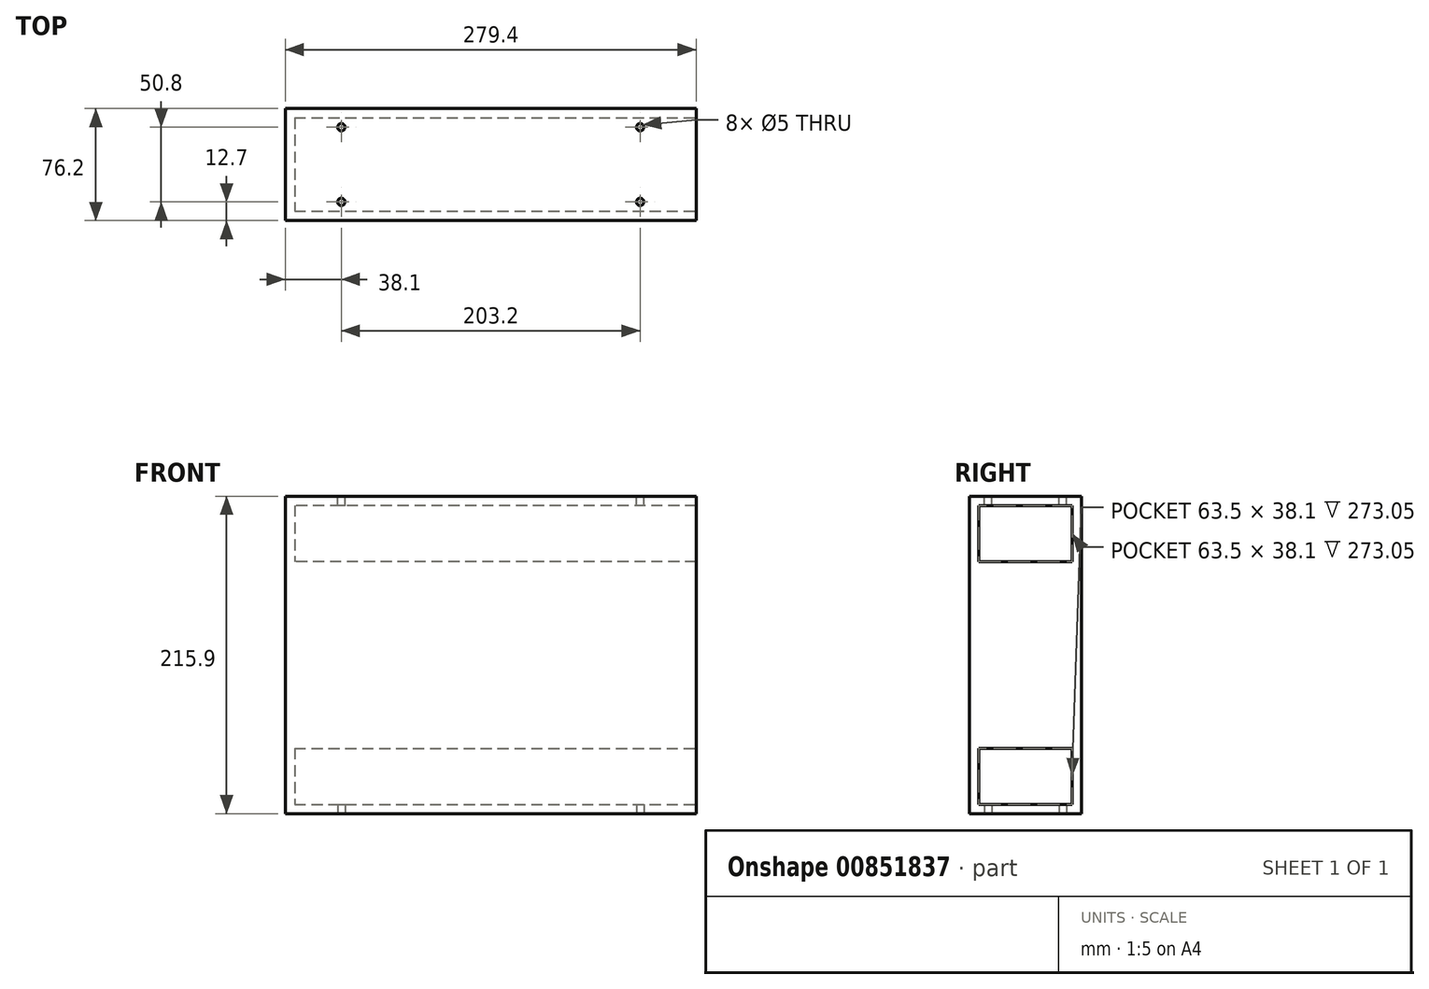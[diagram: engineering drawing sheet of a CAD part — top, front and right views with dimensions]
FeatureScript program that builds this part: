
annotation { "Feature Type Name" : "Feature", "Feature Type Description" : "" }
export const myFeature = defineFeature(function(context is Context, id is Id, definition is map)
    precondition{}
    {
        {
            var Q0;
            Q0=qCreatedBy(makeId("Top.planeOp"),FACE);
            var sketch = newSketch(context, id + "F0", { "sketchPlane" : qUnion([Q0])});
            skLineSegment(sketch, "E0.bottom", {"start": v(139.7, -38.1) * mm, "end": v(-139.7, -38.1) * mm});
            skLineSegment(sketch, "E0.top", {"start": v(139.7, 38.1) * mm, "end": v(-139.7, 38.1) * mm});
            skLineSegment(sketch, "E0.left", {"start": v(139.7, -38.1) * mm, "end": v(139.7, 38.1) * mm});
            skLineSegment(sketch, "E0.right", {"start": v(-139.7, -38.1) * mm, "end": v(-139.7, 38.1) * mm});
            skPoint(sketch, "E0.middle", {"position": v(0, 0) * mm});
            skPoint(sketch, "E1", {"position": v(-133.35, 31.75) * mm});
            skPoint(sketch, "E2", {"position": v(133.35, -31.75) * mm});
            skLineSegment(sketch, "E3.bottom", {"start": v(-133.35, 31.75) * mm, "end": v(133.35, 31.75) * mm});
            skLineSegment(sketch, "E3.top", {"start": v(-133.35, -31.75) * mm, "end": v(133.35, -31.75) * mm});
            skLineSegment(sketch, "E3.left", {"start": v(-133.35, 31.75) * mm, "end": v(-133.35, -31.75) * mm});
            skLineSegment(sketch, "E3.right", {"start": v(133.35, 31.75) * mm, "end": v(133.35, -31.75) * mm});
            skSolve(sketch);
        }
        {
            var Q0;
            Q0 = qSketchRegion(id + "F0", true);
            extrude(context, id + "F1", {"entities" : qUnion([Q0]), "depth" : 38.1 * mm, "offsetDistance" : 25 * mm});
        }
        {
            var Q0;
            Q0=makeQuery(id+"F1.opExtrude","CAP_FACE",FACE,{"disambiguationData":[OSD([sQuery(id+"F0.wireOp",EDGE,"E0.bottom"),sQuery(id+"F0.wireOp",EDGE,"E0.top"),sQuery(id+"F0.wireOp",EDGE,"E0.left"),sQuery(id+"F0.wireOp",EDGE,"E0.right"),sQuery(id+"F0.wireOp",EDGE,"E3.bottom"),sQuery(id+"F0.wireOp",EDGE,"E3.top"),sQuery(id+"F0.wireOp",EDGE,"E3.left"),sQuery(id+"F0.wireOp",EDGE,"E3.right")])],"isStart":true});
            var sketch = newSketch(context, id + "F2", { "sketchPlane" : qUnion([Q0])});
            skLineSegment(sketch, "E4.bottom", {"start": v(-139.7, 38.1) * mm, "end": v(139.7, 38.1) * mm});
            skLineSegment(sketch, "E4.top", {"start": v(-139.7, -38.1) * mm, "end": v(139.7, -38.1) * mm});
            skLineSegment(sketch, "E4.left", {"start": v(-139.7, 38.1) * mm, "end": v(-139.7, -38.1) * mm});
            skLineSegment(sketch, "E4.right", {"start": v(139.7, 38.1) * mm, "end": v(139.7, -38.1) * mm});
            skSolve(sketch);
        }
        {
            var Q0;
            Q0 = qSketchRegion(id + "F2", true);
            extrude(context, id + "F3", {"entities" : qUnion([Q0]), "operationType" : NewBodyOperationType.ADD, "depth" : 6.35 * mm, "offsetDistance" : 25 * mm});
        }
        {
            var Q0;
            Q0=makeQuery(id+"F1.opExtrude","SWEPT_FACE",FACE,{"disambiguationData":[OSD([sQuery(id+"F0.wireOp",EDGE,"E3.right")])]});
            var sketch = newSketch(context, id + "F4", { "sketchPlane" : qUnion([Q0])});
            skLineSegment(sketch, "E5.bottom", {"start": v(-31.75, 38.1) * mm, "end": v(31.75, 38.1) * mm});
            skLineSegment(sketch, "E5.top", {"start": v(-31.75, 0) * mm, "end": v(31.75, 0) * mm});
            skLineSegment(sketch, "E5.left", {"start": v(-31.75, 38.1) * mm, "end": v(-31.75, 0) * mm});
            skLineSegment(sketch, "E5.right", {"start": v(31.75, 38.1) * mm, "end": v(31.75, 0) * mm});
            skSolve(sketch);
        }
        {
            var Q0;
            Q0 = qSketchRegion(id + "F4", true);
            extrude(context, id + "F5", {"entities" : qUnion([Q0]), "operationType" : NewBodyOperationType.REMOVE, "oppositeDirection" : true, "depth" : 25 * mm, "offsetDistance" : 25 * mm});
        }
        {
            var Q0;
            Q0=makeQuery(id+"F1.opExtrude","CAP_FACE",FACE,{"disambiguationData":[OSD([sQuery(id+"F0.wireOp",EDGE,"E0.bottom"),sQuery(id+"F0.wireOp",EDGE,"E0.top"),sQuery(id+"F0.wireOp",EDGE,"E0.left"),sQuery(id+"F0.wireOp",EDGE,"E0.right"),sQuery(id+"F0.wireOp",EDGE,"E3.bottom"),sQuery(id+"F0.wireOp",EDGE,"E3.top"),sQuery(id+"F0.wireOp",EDGE,"E3.left"),sQuery(id+"F0.wireOp",EDGE,"E3.right")])],"isStart":false});
            var sketch = newSketch(context, id + "F6", { "sketchPlane" : qUnion([Q0])});
            skLineSegment(sketch, "E6.bottom", {"start": v(139.7, 38.1) * mm, "end": v(-139.7, 38.1) * mm});
            skLineSegment(sketch, "E6.top", {"start": v(139.7, -38.1) * mm, "end": v(-139.7, -38.1) * mm});
            skLineSegment(sketch, "E6.left", {"start": v(139.7, 38.1) * mm, "end": v(139.7, -38.1) * mm});
            skLineSegment(sketch, "E6.right", {"start": v(-139.7, 38.1) * mm, "end": v(-139.7, -38.1) * mm});
            skSolve(sketch);
        }
        {
            var Q0;
            Q0 = qSketchRegion(id + "F6", true);
            extrude(context, id + "F7", {"entities" : qUnion([Q0]), "operationType" : NewBodyOperationType.ADD, "depth" : 127 * mm, "offsetDistance" : 25 * mm});
        }
        {
            var Q0;
            Q0=makeQuery(id+"F7.opExtrude","CAP_FACE",FACE,{"disambiguationData":[OSD([sQuery(id+"F6.wireOp",EDGE,"E6.bottom"),sQuery(id+"F6.wireOp",EDGE,"E6.top"),sQuery(id+"F6.wireOp",EDGE,"E6.left"),sQuery(id+"F6.wireOp",EDGE,"E6.right")])],"isStart":false});
            var sketch = newSketch(context, id + "F8", { "sketchPlane" : qUnion([Q0])});
            skLineSegment(sketch, "E7.bottom", {"start": v(139.7, 38.1) * mm, "end": v(-139.7, 38.1) * mm});
            skLineSegment(sketch, "E7.top", {"start": v(139.7, -38.1) * mm, "end": v(-139.7, -38.1) * mm});
            skLineSegment(sketch, "E7.left", {"start": v(139.7, 38.1) * mm, "end": v(139.7, -38.1) * mm});
            skLineSegment(sketch, "E7.right", {"start": v(-139.7, 38.1) * mm, "end": v(-139.7, -38.1) * mm});
            skPoint(sketch, "E8", {"position": v(133.35, 31.75) * mm});
            skPoint(sketch, "E9", {"position": v(-133.35, -31.75) * mm});
            skLineSegment(sketch, "E10.bottom", {"start": v(133.35, 31.75) * mm, "end": v(-133.35, 31.75) * mm});
            skLineSegment(sketch, "E10.top", {"start": v(133.35, -31.75) * mm, "end": v(-133.35, -31.75) * mm});
            skLineSegment(sketch, "E10.left", {"start": v(133.35, 31.75) * mm, "end": v(133.35, -31.75) * mm});
            skLineSegment(sketch, "E10.right", {"start": v(-133.35, 31.75) * mm, "end": v(-133.35, -31.75) * mm});
            skSolve(sketch);
        }
        {
            var Q0;
            Q0 = qSketchRegion(id + "F8", true);
            extrude(context, id + "F9", {"entities" : qUnion([Q0]), "operationType" : NewBodyOperationType.ADD, "depth" : 38.1 * mm, "offsetDistance" : 25 * mm});
        }
        {
            var Q0;
            Q0=makeQuery(id+"F9.opExtrude","SWEPT_FACE",FACE,{"disambiguationData":[OSD([sQuery(id+"F8.wireOp",EDGE,"E10.left")])]});
            var sketch = newSketch(context, id + "F10", { "sketchPlane" : qUnion([Q0])});
            skLineSegment(sketch, "E11.bottom", {"start": v(-31.75, 203.2) * mm, "end": v(31.75, 203.2) * mm});
            skLineSegment(sketch, "E11.top", {"start": v(-31.75, 165.1) * mm, "end": v(31.75, 165.1) * mm});
            skLineSegment(sketch, "E11.left", {"start": v(-31.75, 203.2) * mm, "end": v(-31.75, 165.1) * mm});
            skLineSegment(sketch, "E11.right", {"start": v(31.75, 203.2) * mm, "end": v(31.75, 165.1) * mm});
            skSolve(sketch);
        }
        {
            var Q0;
            Q0 = qSketchRegion(id + "F10", true);
            extrude(context, id + "F11", {"entities" : qUnion([Q0]), "operationType" : NewBodyOperationType.REMOVE, "oppositeDirection" : true, "depth" : 25 * mm, "offsetDistance" : 25 * mm});
        }
        {
            var Q0;
            Q0=makeQuery(id+"F9.opExtrude","CAP_FACE",FACE,{"disambiguationData":[OSD([sQuery(id+"F8.wireOp",EDGE,"E7.bottom"),sQuery(id+"F8.wireOp",EDGE,"E7.top"),sQuery(id+"F8.wireOp",EDGE,"E7.left"),sQuery(id+"F8.wireOp",EDGE,"E7.right"),sQuery(id+"F8.wireOp",EDGE,"E10.bottom"),sQuery(id+"F8.wireOp",EDGE,"E10.top"),sQuery(id+"F8.wireOp",EDGE,"E10.left"),sQuery(id+"F8.wireOp",EDGE,"E10.right")])],"isStart":false});
            var sketch = newSketch(context, id + "F12", { "sketchPlane" : qUnion([Q0])});
            skLineSegment(sketch, "E12.bottom", {"start": v(139.7, 38.1) * mm, "end": v(-139.7, 38.1) * mm});
            skLineSegment(sketch, "E12.top", {"start": v(139.7, -38.1) * mm, "end": v(-139.7, -38.1) * mm});
            skLineSegment(sketch, "E12.left", {"start": v(139.7, 38.1) * mm, "end": v(139.7, -38.1) * mm});
            skLineSegment(sketch, "E12.right", {"start": v(-139.7, 38.1) * mm, "end": v(-139.7, -38.1) * mm});
            skSolve(sketch);
        }
        {
            var Q0;
            Q0 = qSketchRegion(id + "F12", true);
            extrude(context, id + "F13", {"entities" : qUnion([Q0]), "operationType" : NewBodyOperationType.ADD, "depth" : 6.35 * mm, "offsetDistance" : 25 * mm});
        }
        {
            var Q0;
            Q0=makeQuery(id+"F13.opExtrude","CAP_FACE",FACE,{"disambiguationData":[OSD([sQuery(id+"F12.wireOp",EDGE,"E12.bottom"),sQuery(id+"F12.wireOp",EDGE,"E12.top"),sQuery(id+"F12.wireOp",EDGE,"E12.left"),sQuery(id+"F12.wireOp",EDGE,"E12.right")])],"isStart":false});
            var sketch = newSketch(context, id + "F14", { "sketchPlane" : qUnion([Q0])});
            skPoint(sketch, "E13", {"position": v(101.6, 25.4) * mm});
            skPoint(sketch, "E14", {"position": v(-101.6, -25.4) * mm});
            skPoint(sketch, "E15", {"position": v(101.6, -25.4) * mm});
            skPoint(sketch, "E16", {"position": v(-101.6, 25.4) * mm});
            skCircle(sketch, "E17", {"center": v(101.6, 25.4) * mm, "radius": 2.5 * mm});
            skCircle(sketch, "E18", {"center": v(101.6, -25.4) * mm, "radius": 2.5 * mm});
            skCircle(sketch, "E19", {"center": v(-101.6, 25.4) * mm, "radius": 2.5 * mm});
            skCircle(sketch, "E20", {"center": v(-101.6, -25.4) * mm, "radius": 2.5 * mm});
            skSolve(sketch);
        }
        {
            var Q0;
            Q0 = qSketchRegion(id + "F14", true);
            var Q1;
            Q1=makeQuery(id+"F13.opExtrude","CAP_FACE",FACE,{"disambiguationData":[OSD([sQuery(id+"F12.wireOp",EDGE,"E12.bottom"),sQuery(id+"F12.wireOp",EDGE,"E12.top"),sQuery(id+"F12.wireOp",EDGE,"E12.left"),sQuery(id+"F12.wireOp",EDGE,"E12.right")])],"isStart":true});
            extrude(context, id + "F15", {"entities" : qUnion([Q0]), "operationType" : NewBodyOperationType.REMOVE, "endBound" : BoundingType.UP_TO_SURFACE, "oppositeDirection" : true, "depth" : 25 * mm, "endBoundEntityFace" : qUnion([Q1]), "offsetDistance" : 25 * mm});
        }
        {
            var Q0;
            Q0=makeQuery(id+"F3.opExtrude","CAP_FACE",FACE,{"disambiguationData":[OSD([sQuery(id+"F2.wireOp",EDGE,"E4.bottom"),sQuery(id+"F2.wireOp",EDGE,"E4.top"),sQuery(id+"F2.wireOp",EDGE,"E4.left"),sQuery(id+"F2.wireOp",EDGE,"E4.right")])],"isStart":false});
            var sketch = newSketch(context, id + "F16", { "sketchPlane" : qUnion([Q0])});
            skPoint(sketch, "E21", {"position": v(101.6, -25.4) * mm});
            skPoint(sketch, "E22", {"position": v(-101.6, 25.4) * mm});
            skPoint(sketch, "E23", {"position": v(101.6, 25.4) * mm});
            skPoint(sketch, "E24", {"position": v(-101.6, -25.4) * mm});
            skCircle(sketch, "E25", {"center": v(-101.6, -25.4) * mm, "radius": 2.5 * mm});
            skCircle(sketch, "E26", {"center": v(-101.6, 25.4) * mm, "radius": 2.5 * mm});
            skCircle(sketch, "E27", {"center": v(101.6, -25.4) * mm, "radius": 2.5 * mm});
            skCircle(sketch, "E28", {"center": v(101.6, 25.4) * mm, "radius": 2.5 * mm});
            skSolve(sketch);
        }
        {
            var Q0;
            Q0 = qSketchRegion(id + "F16", true);
            var Q1;
            Q1=makeQuery(id+"F5.boolean.opBoolean","MERGE",FACE,{"derivedFrom":[makeQuery(id+"F3.opExtrude","CAP_FACE",FACE,{"disambiguationData":[OSD([sQuery(id+"F2.wireOp",EDGE,"E4.bottom"),sQuery(id+"F2.wireOp",EDGE,"E4.top"),sQuery(id+"F2.wireOp",EDGE,"E4.left"),sQuery(id+"F2.wireOp",EDGE,"E4.right")])],"isStart":true}),makeQuery(id+"F5.opExtrude","SWEPT_FACE",FACE,{"disambiguationData":[OSD([sQuery(id+"F4.wireOp",EDGE,"E5.top")])]})]});
            extrude(context, id + "F17", {"entities" : qUnion([Q0]), "operationType" : NewBodyOperationType.REMOVE, "endBound" : BoundingType.UP_TO_SURFACE, "oppositeDirection" : true, "depth" : 25 * mm, "endBoundEntityFace" : qUnion([Q1]), "offsetDistance" : 25 * mm});
        }
    });
